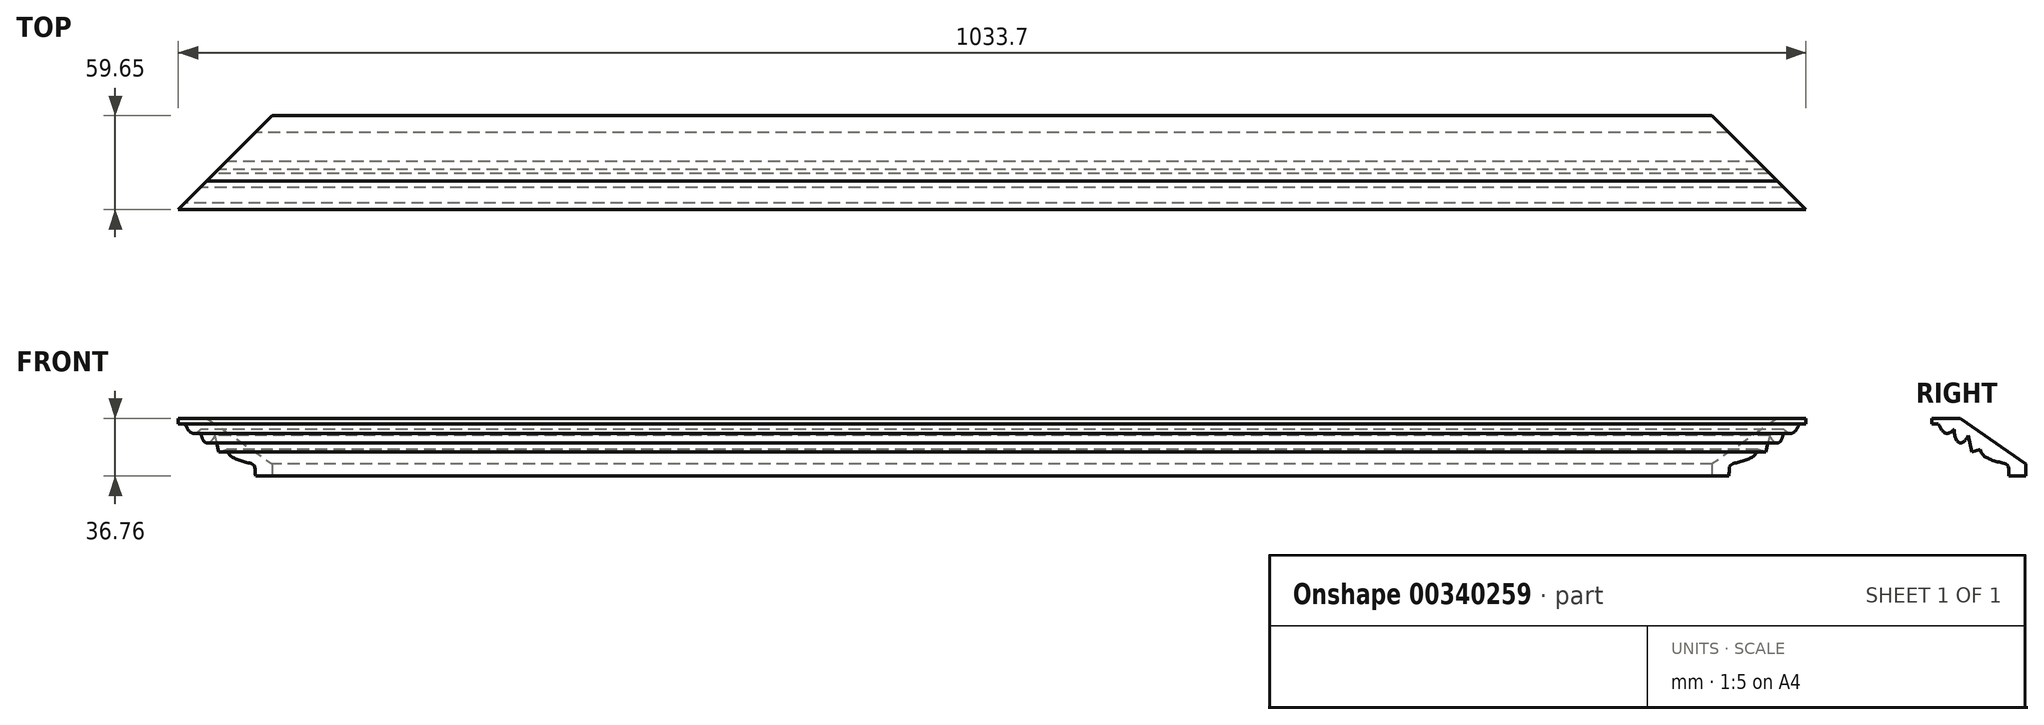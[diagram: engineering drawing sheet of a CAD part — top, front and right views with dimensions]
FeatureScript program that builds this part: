
annotation { "Feature Type Name" : "Feature", "Feature Type Description" : "" }
export const myFeature = defineFeature(function(context is Context, id is Id, definition is map)
    precondition{}
    {
        {
            var Q0;
            Q0=qCreatedBy(makeId("Right.planeOp"),FACE);
            var sketch = newSketch(context, id + "F0", { "sketchPlane" : qUnion([Q0])});
            skLineSegment(sketch, "E0", {"start": v(0, 7.62) * mm, "end": v(-41.61, 36.76) * mm});
            skLineSegment(sketch, "E1", {"start": v(-41.61, 36.76) * mm, "end": v(-59.65, 36.76) * mm});
            skLineSegment(sketch, "E2", {"start": v(-59.65, 36.76) * mm, "end": v(-59.65, 33.27) * mm});
            skLineSegment(sketch, "E3", {"start": v(-59.65, 33.27) * mm, "end": v(-55.58, 33.27) * mm});
            skLineSegment(sketch, "E4", {"start": v(0, 7.62) * mm, "end": v(0, 0) * mm});
            skLineSegment(sketch, "E5", {"start": v(0, 0) * mm, "end": v(-10.67, 0) * mm});
            skFitSpline(sketch, "E6", {"points": [v(-10.67, 0) * mm, v(-11.07, 5.87) * mm, v(-13.33, 7.9) * mm, v(-29.01, 17.09) * mm], "startDerivative": vector(-5.08, 29.03) * mm, "endDerivative": vector(-6.54, 39.72) * mm});
            skLineSegment(sketch, "E7", {"start": v(-29.01, 17.09) * mm, "end": v(-34.16, 15.48) * mm});
            skLineSegment(sketch, "E8", {"start": v(-34.16, 15.48) * mm, "end": v(-36.6, 25.71) * mm});
            skFitSpline(sketch, "E9", {"points": [v(-45.57, 29.68) * mm, v(-52.47, 28.3) * mm, v(-55.58, 33.27) * mm], "startDerivative": vector(-24.15, -24.15) * mm, "endDerivative": vector(-16.65, 31.11) * mm});
            skFitSpline(sketch, "E10", {"points": [v(-45.57, 29.68) * mm, v(-36.6, 25.71) * mm], "startDerivative": vector(2.07, -32.09) * mm, "endDerivative": vector(9.32, 20.18) * mm});
            skSolve(sketch);
        }
        {
            var Q0;
            Q0 = qSketchRegion(id + "F0", true);
            extrude(context, id + "F1", {"entities" : qUnion([Q0]), "depth" : 533.4 * mm, "hasSecondDirection" : true, "secondDirectionOppositeDirection" : true, "secondDirectionDepth" : 533.4 * mm});
        }
        {
            var Q0;
            Q0=qCreatedBy(makeId("Top.planeOp"),FACE);
            var sketch = newSketch(context, id + "F2", { "sketchPlane" : qUnion([Q0])});
            skLineSegment(sketch, "E11", {"start": v(-457.2, 0) * mm, "end": v(457.2, 0) * mm, "construction": true});
            skLineSegment(sketch, "E12", {"start": v(457.2, 0) * mm, "end": v(539.77, 0) * mm});
            skLineSegment(sketch, "E13", {"start": v(539.77, 0) * mm, "end": v(539.77, -82.57) * mm});
            skLineSegment(sketch, "E14", {"start": v(539.77, -82.57) * mm, "end": v(457.2, 0) * mm});
            skLineSegment(sketch, "E15", {"start": v(0, 0) * mm, "end": v(0, -141.75) * mm, "construction": true});
            skLineSegment(sketch, "E16.MirrorCS", {"start": v(-457.2, 0) * mm, "end": v(-539.77, 0) * mm});
            skLineSegment(sketch, "E17.MirrorCS", {"start": v(-539.77, -82.57) * mm, "end": v(-457.2, 0) * mm});
            skLineSegment(sketch, "E18.MirrorCS", {"start": v(-539.77, 0) * mm, "end": v(-539.77, -82.57) * mm});
            skSolve(sketch);
        }
        {
            var Q0;
            Q0 = qSketchRegion(id + "F2", true);
            extrude(context, id + "F3", {"entities" : qUnion([Q0]), "operationType" : NewBodyOperationType.REMOVE, "endBound" : BoundingType.THROUGH_ALL, "depth" : 25.4 * mm});
        }
    });
